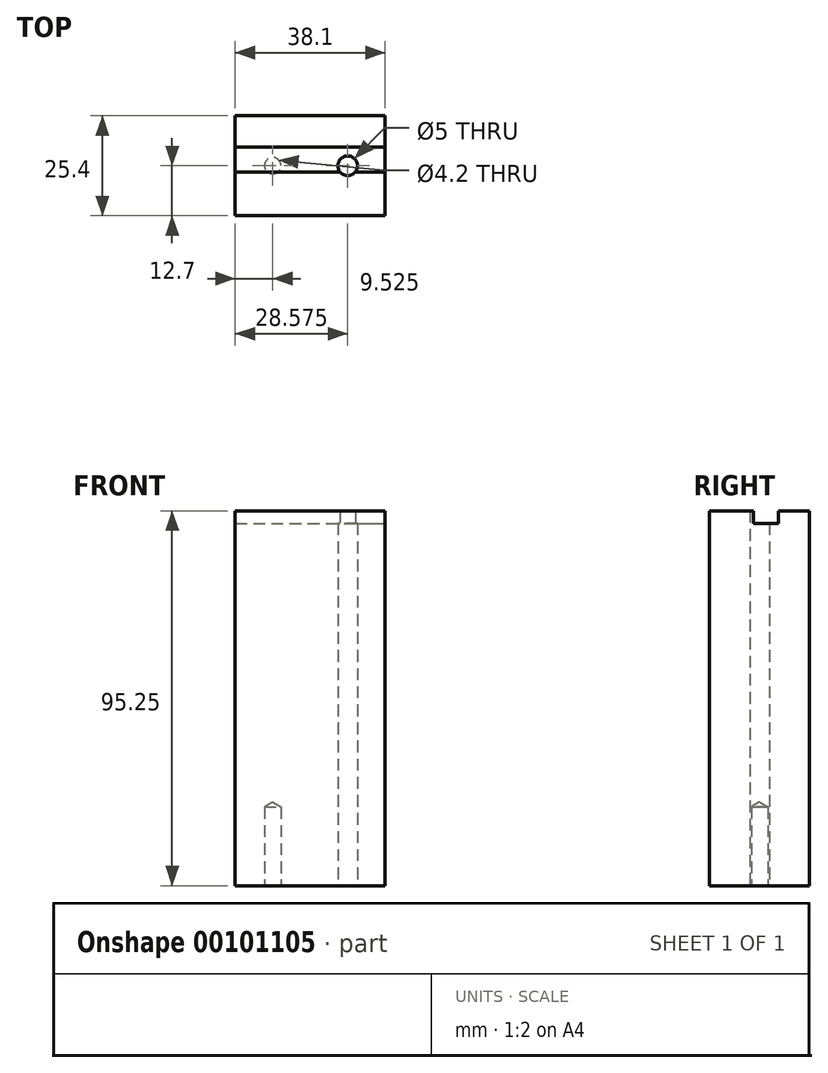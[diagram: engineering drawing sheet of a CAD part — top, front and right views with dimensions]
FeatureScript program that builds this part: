
annotation { "Feature Type Name" : "Feature", "Feature Type Description" : "" }
export const myFeature = defineFeature(function(context is Context, id is Id, definition is map)
    precondition{}
    {
        {
            var Q0;
            Q0=qCreatedBy(makeId("Top.planeOp"),FACE);
            var sketch = newSketch(context, id + "F0", { "sketchPlane" : qUnion([Q0])});
            skLineSegment(sketch, "E0.bottom", {"start": v(19.05, 0) * mm, "end": v(0, 0) * mm});
            skLineSegment(sketch, "E0.top", {"start": v(19.05, 25.4) * mm, "end": v(0, 25.4) * mm});
            skLineSegment(sketch, "E0.left", {"start": v(19.05, 0) * mm, "end": v(19.05, 25.4) * mm, "construction": true});
            skLineSegment(sketch, "E0.right", {"start": v(0, 0) * mm, "end": v(0, 25.4) * mm});
            skLineSegment(sketch, "E1.MirrorCS", {"start": v(19.05, 25.4) * mm, "end": v(38.1, 25.4) * mm});
            skLineSegment(sketch, "E2.MirrorCS", {"start": v(38.1, 0) * mm, "end": v(38.1, 25.4) * mm});
            skLineSegment(sketch, "E3.MirrorCS", {"start": v(19.05, 0) * mm, "end": v(38.1, 0) * mm});
            skCircle(sketch, "E4", {"center": v(9.53, 12.7) * mm, "radius": 2.5 * mm});
            skPoint(sketch, "E4.centerSnap0", {"position": v(0, 12.7) * mm});
            skPoint(sketch, "E4.centerSnap1", {"position": v(9.53, 0) * mm});
            skCircle(sketch, "E5.MirrorC", {"center": v(28.58, 12.7) * mm, "radius": 2.5 * mm});
            skSolve(sketch);
        }
        {
            var Q0;
            Q0=makeQuery(id+"F0.imprint","IMPRINT",FACE,{"disambiguationData":[TD([[makeQuery(id+"F0.imprint","IMPRINT",EDGE,{"derivedFrom":sQuery(id+"F0.wireOp",EDGE,"E0.left")}),-1.0]])]});
            var Q1;
            Q1=makeQuery(id+"F0.imprint","IMPRINT",FACE,{"disambiguationData":[TD([[makeQuery(id+"F0.imprint","IMPRINT",EDGE,{"derivedFrom":sQuery(id+"F0.wireOp",EDGE,"E0.bottom")}),-1.0]])]});
            var Q2;
            Q2=makeQuery(id+"F0.imprint","IMPRINT",FACE,{"disambiguationData":[TD([[makeQuery(id+"F0.imprint","IMPRINT",EDGE,{"derivedFrom":sQuery(id+"F0.wireOp",EDGE,"E4")}),1.0]])]});
            var Q3;
            Q3=makeQuery(id+"F0.imprint","IMPRINT",FACE,{"disambiguationData":[TD([[makeQuery(id+"F0.imprint","IMPRINT",EDGE,{"derivedFrom":sQuery(id+"F0.wireOp",EDGE,"E5.MirrorC")}),-1.0]])]});
            extrude(context, id + "F1", {"entities" : qUnion([Q0, Q1, Q2, Q3]), "depth" : 95.25 * mm});
        }
        {
            var Q0;
            Q0=makeQuery(id+"F1.opExtrude","SWEPT_FACE",FACE,{"disambiguationData":[OSD([sQuery(id+"F0.wireOp",EDGE,"E2.MirrorCS")])]});
            var sketch = newSketch(context, id + "F2", { "sketchPlane" : qUnion([Q0])});
            skLineSegment(sketch, "E6", {"start": v(25.4, 95.25) * mm, "end": v(17.46, 95.25) * mm});
            skLineSegment(sketch, "E7.bottom", {"start": v(17.46, 95.25) * mm, "end": v(11.11, 95.25) * mm});
            skLineSegment(sketch, "E7.top", {"start": v(17.46, 92.08) * mm, "end": v(11.11, 92.08) * mm});
            skLineSegment(sketch, "E7.left", {"start": v(17.46, 95.25) * mm, "end": v(17.46, 92.08) * mm});
            skLineSegment(sketch, "E7.right", {"start": v(11.11, 95.25) * mm, "end": v(11.11, 92.08) * mm});
            skSolve(sketch);
        }
        {
            var Q0;
            Q0=makeQuery(id+"F2.imprint","IMPRINT",FACE,{"disambiguationData":[TD([[makeQuery(id+"F2.imprint","IMPRINT",EDGE,{"derivedFrom":sQuery(id+"F2.wireOp",EDGE,"E7.bottom")}),-1.0]])]});
            extrude(context, id + "F3", {"entities" : qUnion([Q0]), "operationType" : NewBodyOperationType.REMOVE, "endBound" : BoundingType.THROUGH_ALL, "oppositeDirection" : true, "depth" : 25.4 * mm});
        }
        {
            var Q0;
            Q0=sQuery(id+"F0.wireOp",VERTEX,"E4.center");
            var Q1;
            Q1=sQuery(id+"F0.wireOp",VERTEX,"E5.MirrorC.center");
            var Q2;
            Q2=makeQuery(id+"F1.opExtrude","SWEPT_BODY",BODY,{"disambiguationData":[OSD([sQuery(id+"F0.wireOp",EDGE,"E0.bottom"),sQuery(id+"F0.wireOp",EDGE,"E0.top"),sQuery(id+"F0.wireOp",EDGE,"E0.right"),sQuery(id+"F0.wireOp",EDGE,"E1.MirrorCS"),sQuery(id+"F0.wireOp",EDGE,"E2.MirrorCS"),sQuery(id+"F0.wireOp",EDGE,"E3.MirrorCS")])]});
            hole(context, id + "F4", {"style" : HoleStyle.SIMPLE, "endStyle" : HoleEndStyle.BLIND, "oppositeDirection" : true, "standardTappedOrClearance" : lookupTablePath({ "standard" : "ISO", "engagement" : "75%", "pitch" : "0.8 mm", "size" : "M5", "type" : "Tapped" }), "standardBlindInLast" : lookupTablePath({ "standard" : "ISO", "engagement" : "75%", "pitch" : "0.8 mm", "size" : "M5", "type" : "Tapped" }), "holeDiameter" : 4.2 * mm, "holeDepth" : 20 * mm, "locations" : qUnion([Q0, Q1]), "scope" : qUnion([Q2]), "majorDiameter" : 5 * mm});
        }
    });
